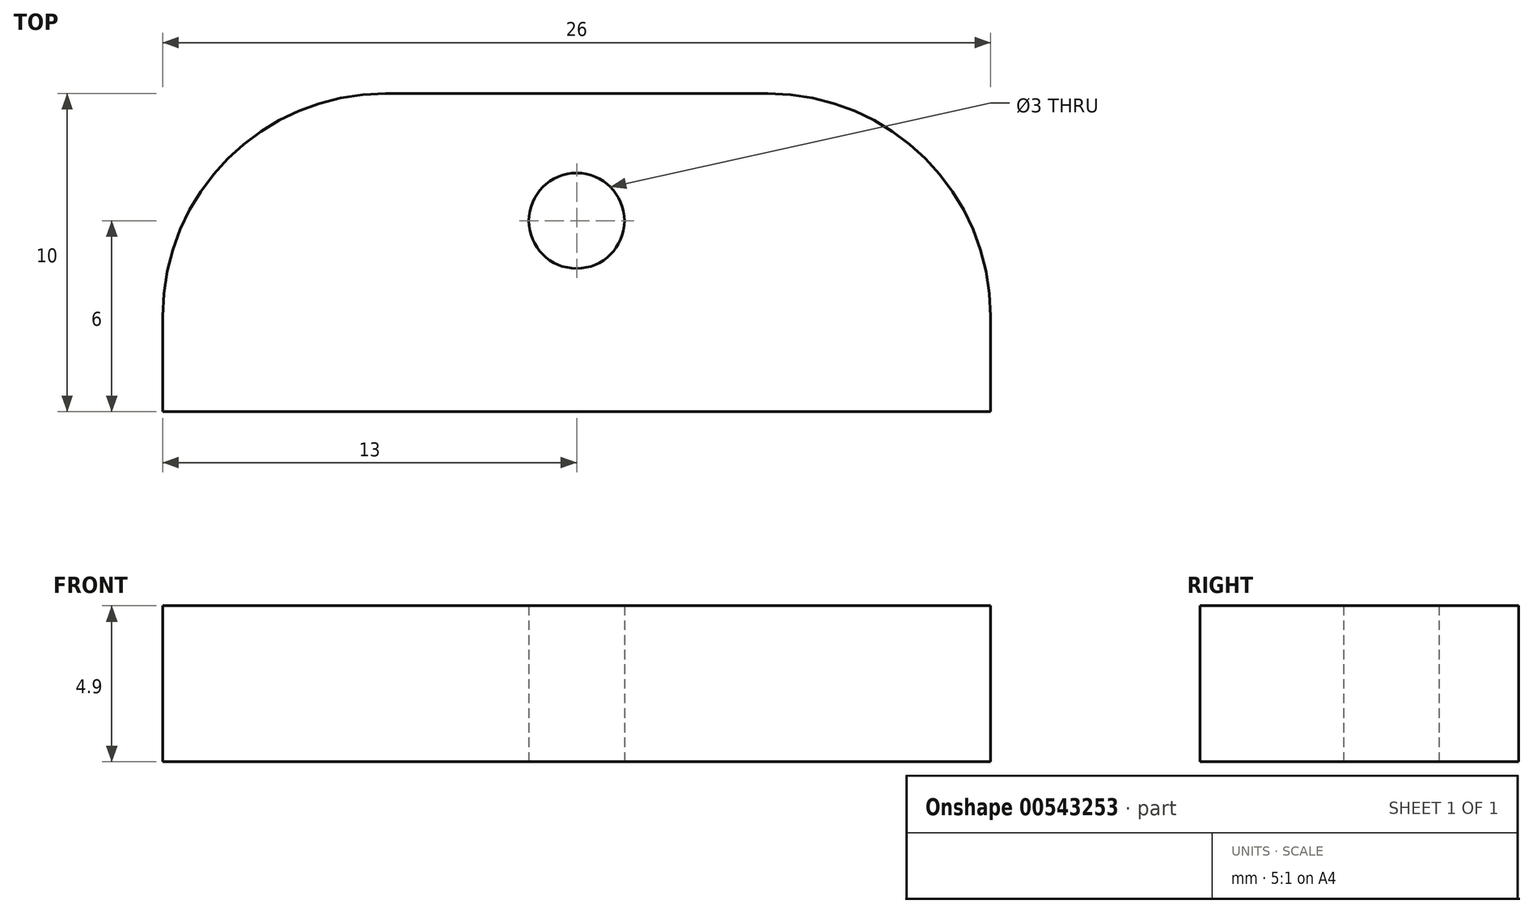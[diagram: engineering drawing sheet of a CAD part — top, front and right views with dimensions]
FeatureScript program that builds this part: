
annotation { "Feature Type Name" : "Feature", "Feature Type Description" : "" }
export const myFeature = defineFeature(function(context is Context, id is Id, definition is map)
    precondition{}
    {
        {
            var Q0;
            Q0=qCreatedBy(makeId("Top.planeOp"),FACE);
            var sketch = newSketch(context, id + "F0", { "sketchPlane" : qUnion([Q0])});
            skLineSegment(sketch, "E0.0", {"start": v(20.9, 16.5) * mm, "end": v(20.9, 30.9) * mm});
            skLineSegment(sketch, "E0.1", {"start": v(17.9, 16.5) * mm, "end": v(20.9, 16.5) * mm});
            skLineSegment(sketch, "E0.2", {"start": v(17.9, 13.2) * mm, "end": v(17.9, 16.5) * mm});
            skLineSegment(sketch, "E0.3", {"start": v(20.9, 11.7) * mm, "end": v(19.4, 11.7) * mm});
            skLineSegment(sketch, "E0.4", {"start": v(20.9, 4.9) * mm, "end": v(20.9, 11.7) * mm});
            skLineSegment(sketch, "E0.6", {"start": v(14.1, 4.9) * mm, "end": v(20.9, 4.9) * mm});
            skLineSegment(sketch, "E0.7", {"start": v(14.1, 6.4) * mm, "end": v(14.1, 4.9) * mm});
            skLineSegment(sketch, "E0.8", {"start": v(9.3, 7.9) * mm, "end": v(12.6, 7.9) * mm});
            skLineSegment(sketch, "E0.9", {"start": v(9.3, 4.9) * mm, "end": v(9.3, 7.9) * mm});
            skLineSegment(sketch, "E0.19", {"start": v(-5.1, 4.9) * mm, "end": v(9.3, 4.9) * mm});
            skLineSegment(sketch, "E1.0", {"start": v(25.9, 4.9) * mm, "end": v(25.9, 30.9) * mm});
            skLineSegment(sketch, "E2", {"start": v(-5.1, -0.1) * mm, "end": v(-5.1, 4.9) * mm});
            skLineSegment(sketch, "E3", {"start": v(25.9, 30.9) * mm, "end": v(20.9, 30.9) * mm});
            skLineSegment(sketch, "E4", {"start": v(25.9, 4.9) * mm, "end": v(20.9, -0.1) * mm});
            skLineSegment(sketch, "E5", {"start": v(19.4, 11.7) * mm, "end": v(17.9, 13.2) * mm});
            skLineSegment(sketch, "E6", {"start": v(14.1, 6.4) * mm, "end": v(12.6, 7.9) * mm});
            skLineSegment(sketch, "E7", {"start": v(20.9, -0.1) * mm, "end": v(20.9, -12.1) * mm});
            skLineSegment(sketch, "E8", {"start": v(20.9, -12.1) * mm, "end": v(-5.1, -12.1) * mm});
            skLineSegment(sketch, "E9", {"start": v(-5.1, -12.1) * mm, "end": v(-5.1, -0.1) * mm});
            skPoint(sketch, "E10", {"position": v(7.9, -8.1) * mm});
            skPoint(sketch, "E10.positionSnap0", {"position": v(20.9, -6.1) * mm});
            skPoint(sketch, "E10.positionSnap1", {"position": v(7.9, -12.1) * mm});
            skLineSegment(sketch, "E11", {"start": v(-5.1, -0.1) * mm, "end": v(20.9, -0.1) * mm});
            skSolve(sketch);
        }
        {
            var Q0;
            Q0=makeQuery(id+"F0.imprint","IMPRINT",FACE,{"disambiguationData":[TD([[makeQuery(id+"F0.imprint","IMPRINT",EDGE,{"derivedFrom":sQuery(id+"F0.wireOp",EDGE,"E0.0")}),-1.0]])]});
            extrude(context, id + "F1", {"entities" : qUnion([Q0]), "depth" : 10 * mm, "offsetDistance" : 25 * mm});
        }
        {
            var Q0;
            Q0=makeQuery(id+"F0.imprint","IMPRINT",FACE,{"disambiguationData":[TD([[makeQuery(id+"F0.imprint","IMPRINT",EDGE,{"derivedFrom":sQuery(id+"F0.wireOp",EDGE,"E7")}),-1.0]])]});
            extrude(context, id + "F2", {"entities" : qUnion([Q0]), "operationType" : NewBodyOperationType.ADD, "depth" : 5 * mm, "offsetDistance" : 25 * mm});
        }
        {
            var Q0;
            Q0=sQuery(id+"F0.wireOp",VERTEX,"E10");
            var Q1;
            Q1=makeQuery(id+"F1.opExtrude","SWEPT_BODY",BODY,{"disambiguationData":[OSD([sQuery(id+"F0.wireOp",EDGE,"E0.0"),sQuery(id+"F0.wireOp",EDGE,"E0.1"),sQuery(id+"F0.wireOp",EDGE,"E0.2"),sQuery(id+"F0.wireOp",EDGE,"E0.3"),sQuery(id+"F0.wireOp",EDGE,"E0.4"),sQuery(id+"F0.wireOp",EDGE,"E0.6"),sQuery(id+"F0.wireOp",EDGE,"E0.7"),sQuery(id+"F0.wireOp",EDGE,"E0.8"),sQuery(id+"F0.wireOp",EDGE,"E0.9"),sQuery(id+"F0.wireOp",EDGE,"E0.19"),sQuery(id+"F0.wireOp",EDGE,"E1.0"),sQuery(id+"F0.wireOp",EDGE,"E2"),sQuery(id+"F0.wireOp",EDGE,"E3"),sQuery(id+"F0.wireOp",EDGE,"E4"),sQuery(id+"F0.wireOp",EDGE,"E5"),sQuery(id+"F0.wireOp",EDGE,"E6"),sQuery(id+"F0.wireOp",EDGE,"E11")])]});
            hole(context, id + "F3", {"style" : HoleStyle.SIMPLE, "endStyle" : HoleEndStyle.THROUGH, "oppositeDirection" : true, "holeDiameter" : 3 * mm, "isTappedThrough" : true, "tappedDepth" : 12 * mm, "tapClearance" : 3, "locations" : qUnion([Q0]), "scope" : qUnion([Q1])});
        }
        {
            var Q0;
            Q0=qCreatedBy(makeId("Top.planeOp"),FACE);
            var sketch = newSketch(context, id + "F4", { "sketchPlane" : qUnion([Q0])});
            skLineSegment(sketch, "E12.0", {"start": v(13.9, -12.2) * mm, "end": v(1.9, -12.2) * mm});
            skLineSegment(sketch, "E13.0", {"start": v(20.9, -22.2) * mm, "end": v(-5.1, -22.2) * mm});
            skLineSegment(sketch, "E14", {"start": v(-5.1, -19.2) * mm, "end": v(-5.1, -22.2) * mm});
            skLineSegment(sketch, "E15", {"start": v(20.9, -19.2) * mm, "end": v(20.9, -22.2) * mm});
            skPoint(sketch, "E16.visualSharp", {"position": v(-5.1, -12.2) * mm});
            skArc(sketch, "E16.filletArc", {"start": v(1.9, -12.2) * mm, "mid": v(-3.05, -14.25) * mm, "end": v(-5.1, -19.2) * mm});
            skPoint(sketch, "E17.visualSharp", {"position": v(20.9, -12.2) * mm});
            skArc(sketch, "E17.filletArc", {"start": v(20.9, -19.2) * mm, "mid": v(18.85, -14.25) * mm, "end": v(13.9, -12.2) * mm});
            skPoint(sketch, "E18", {"position": v(7.9, -16.2) * mm});
            skSolve(sketch);
        }
        {
            var Q0;
            Q0=makeQuery(id+"F4.imprint","IMPRINT",FACE,{"disambiguationData":[TD([[makeQuery(id+"F4.imprint","IMPRINT",EDGE,{"derivedFrom":sQuery(id+"F4.wireOp",EDGE,"E12.0")}),1.0]])]});
            extrude(context, id + "F5", {"entities" : qUnion([Q0]), "depth" : 4.9 * mm, "offsetDistance" : 25 * mm});
        }
        {
            var Q0;
            Q0=sQuery(id+"F4.wireOp",VERTEX,"E18");
            var Q1;
            Q1=makeQuery(id+"F5.opExtrude","SWEPT_BODY",BODY,{"disambiguationData":[OSD([sQuery(id+"F4.wireOp",EDGE,"E12.0"),sQuery(id+"F4.wireOp",EDGE,"E13.0"),sQuery(id+"F4.wireOp",EDGE,"E14"),sQuery(id+"F4.wireOp",EDGE,"E15"),sQuery(id+"F4.wireOp",EDGE,"E16.filletArc"),sQuery(id+"F4.wireOp",EDGE,"E17.filletArc")])]});
            hole(context, id + "F6", {"style" : HoleStyle.SIMPLE, "endStyle" : HoleEndStyle.THROUGH, "oppositeDirection" : true, "holeDiameter" : 3 * mm, "majorDiameter" : 5 * mm, "isTappedThrough" : true, "tappedDepth" : 12 * mm, "tapClearance" : 3, "locations" : qUnion([Q0]), "scope" : qUnion([Q1])});
        }
        {
            var Q0;
            Q0=makeQuery(id+"F1.opExtrude","SWEPT_BODY",BODY,{"disambiguationData":[OSD([sQuery(id+"F0.wireOp",EDGE,"E0.0"),sQuery(id+"F0.wireOp",EDGE,"E0.1"),sQuery(id+"F0.wireOp",EDGE,"E0.2"),sQuery(id+"F0.wireOp",EDGE,"E0.3"),sQuery(id+"F0.wireOp",EDGE,"E0.4"),sQuery(id+"F0.wireOp",EDGE,"E0.6"),sQuery(id+"F0.wireOp",EDGE,"E0.7"),sQuery(id+"F0.wireOp",EDGE,"E0.8"),sQuery(id+"F0.wireOp",EDGE,"E0.9"),sQuery(id+"F0.wireOp",EDGE,"E0.19"),sQuery(id+"F0.wireOp",EDGE,"E1.0"),sQuery(id+"F0.wireOp",EDGE,"E2"),sQuery(id+"F0.wireOp",EDGE,"E3"),sQuery(id+"F0.wireOp",EDGE,"E4"),sQuery(id+"F0.wireOp",EDGE,"E5"),sQuery(id+"F0.wireOp",EDGE,"E6"),sQuery(id+"F0.wireOp",EDGE,"E11")])]});
            deleteBodies(context, id + "F7", {"entities" : qUnion([Q0])});
        }
    });
